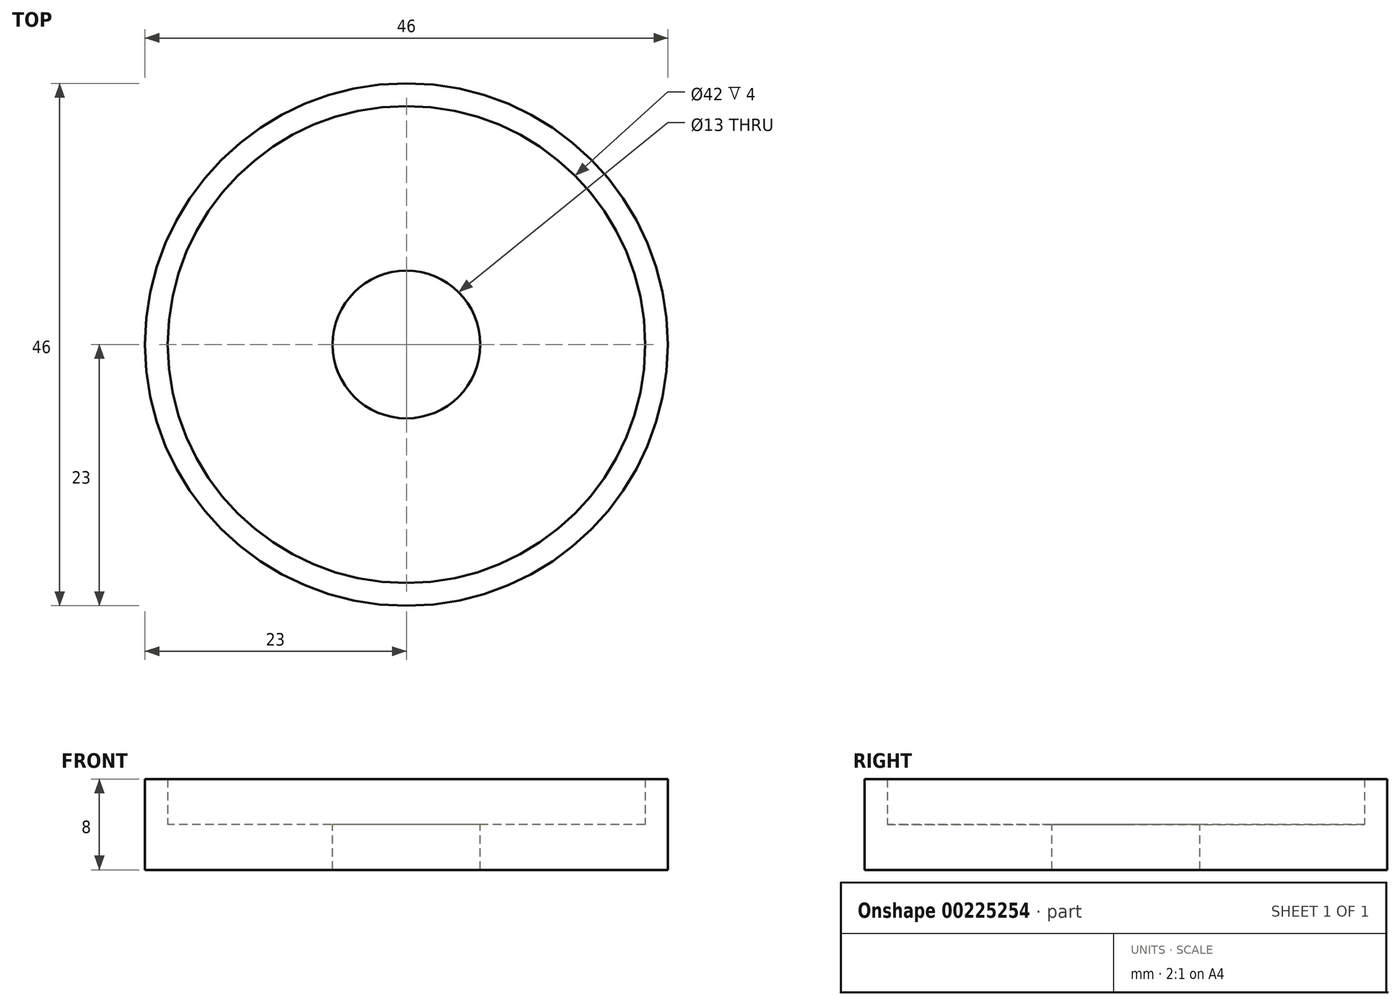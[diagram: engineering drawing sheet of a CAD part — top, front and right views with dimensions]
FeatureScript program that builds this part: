
annotation { "Feature Type Name" : "Feature", "Feature Type Description" : "" }
export const myFeature = defineFeature(function(context is Context, id is Id, definition is map)
    precondition{}
    {
        {
            var Q0;
            Q0=qCreatedBy(makeId("Top.planeOp"),FACE);
            var sketch = newSketch(context, id + "F0", { "sketchPlane" : qUnion([Q0])});
            skCircle(sketch, "E0", {"center": v(0, 0) * mm, "radius": 23 * mm});
            skSolve(sketch);
        }
        {
            var Q0;
            Q0 = qSketchRegion(id + "F0", true);
            extrude(context, id + "F1", {"entities" : qUnion([Q0]), "depth" : 4 * mm});
        }
        {
            var Q0;
            Q0=makeQuery(id+"F1.opExtrude","CAP_FACE",FACE,{"disambiguationData":[OSD([sQuery(id+"F0.wireOp",EDGE,"E0")])],"isStart":false});
            var sketch = newSketch(context, id + "F2", { "sketchPlane" : qUnion([Q0])});
            skCircle(sketch, "E1.0", {"center": v(0, 0) * mm, "radius": 23 * mm});
            skCircle(sketch, "E2", {"center": v(0, 0) * mm, "radius": 21 * mm});
            skSolve(sketch);
        }
        {
            var Q0;
            Q0 = qSketchRegion(id + "F2", true);
            extrude(context, id + "F3", {"entities" : qUnion([Q0]), "operationType" : NewBodyOperationType.ADD, "depth" : 4 * mm});
        }
        {
            var Q0;
            Q0=makeQuery(id+"F1.opExtrude","CAP_FACE",FACE,{"disambiguationData":[OSD([sQuery(id+"F0.wireOp",EDGE,"E0")])],"isStart":false});
            var sketch = newSketch(context, id + "F4", { "sketchPlane" : qUnion([Q0])});
            skCircle(sketch, "E3", {"center": v(0, 0) * mm, "radius": 6.5 * mm});
            skSolve(sketch);
        }
        {
            var Q0;
            Q0 = qSketchRegion(id + "F4", true);
            extrude(context, id + "F5", {"entities" : qUnion([Q0]), "operationType" : NewBodyOperationType.REMOVE, "endBound" : BoundingType.UP_TO_NEXT, "oppositeDirection" : true, "depth" : 25 * mm});
        }
    });
